# Revit family: P2815D_Adjustable_Brace_Fitting
name_source: partatom
category: Generic Models
units: mm (PartAtom-declared; Revit-internal decimal feet)

## family parameters
Always vertical = No
Can host rebar = No
Cut with Voids When Loaded = No
OmniClass Number = 23.80.30.17.17
OmniClass Title = Cable Trays and Horizontal Racks
Part Type = Normal
Room Calculation Point = No
Round Connector Dimension = Use Diameter
Shared = No
Work Plane-Based = Yes

## types (4) — shared parameters
Default Elevation = 48 "
Description = P2815D - Adjustable Brace Fitting
Disclaimer = http://www.unistrut.us
Height = 0.25 "
L_half = 4 "
Length = 8 "
Manufacturer = Atkore Unistrut
Model = P2815D
Salsify ID1 = US-P2815D
Type Comments = 80_77_27_15
URL = https://www.atkore.com
Width = 1.625 "

## per-type parameters (varying)
| type | Material | Power-Strut Part Number | UPC | Weight |
| P2815D HG | Hot Dip Galvanized |  | "0" | 5.26 lbm |
| P2815D EG | Electro Galvanized | PS 9401 EG | "78636403256" | 4.97 lbm |
| P2815D GR | Green |  | "0" | 4.97 lbm |
| P2815D ZD | Zinc Dichromate |  | "0" | 4.97 lbm |

note: column(s) folded — value = type name in every type: Part Number

## geometry (parser evidence)
native form markers: Sweep x6
no freeform markers — native parametric forms only
